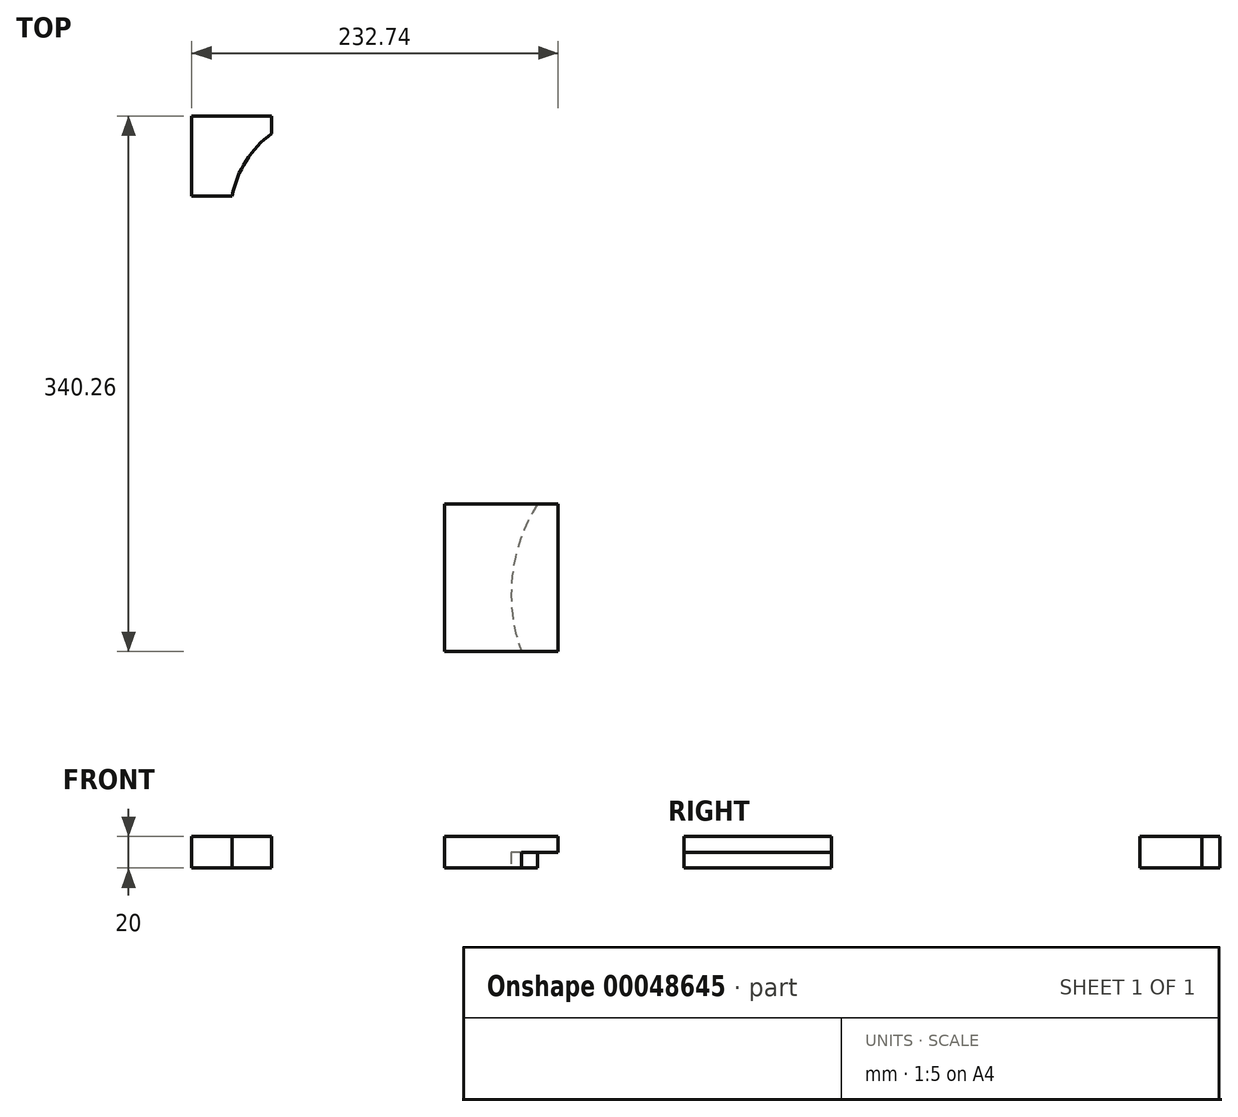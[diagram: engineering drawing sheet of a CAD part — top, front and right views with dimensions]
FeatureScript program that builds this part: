
annotation { "Feature Type Name" : "Feature", "Feature Type Description" : "" }
export const myFeature = defineFeature(function(context is Context, id is Id, definition is map)
    precondition{}
    {
        {
            assignVariable(context, id + "F0", {"name" : "teste", "anyValue" : 20});
        }
        {
            var Q0;
            Q0=qCreatedBy(makeId("Top.planeOp"),FACE);
            var sketch = newSketch(context, id + "F1", { "sketchPlane" : qUnion([Q0])});
            skLineSegment(sketch, "E0", {"start": v(-15.73, 9.77) * mm, "end": v(-15.73, -41.03) * mm});
            skLineSegment(sketch, "E1", {"start": v(-15.73, -41.03) * mm, "end": v(35.07, -41.03) * mm});
            skLineSegment(sketch, "E2", {"start": v(35.07, -41.03) * mm, "end": v(35.07, 9.77) * mm});
            skLineSegment(sketch, "E3", {"start": v(35.07, 9.77) * mm, "end": v(-15.73, 9.77) * mm});
            skLineSegment(sketch, "E4", {"start": v(178.54, 68) * mm, "end": v(178.54, -33.6) * mm});
            skLineSegment(sketch, "E5", {"start": v(178.54, -33.6) * mm, "end": v(407.14, -33.6) * mm});
            skLineSegment(sketch, "E6", {"start": v(407.14, -33.6) * mm, "end": v(407.14, 41.42) * mm});
            skLineSegment(sketch, "E7", {"start": v(407.14, 41.42) * mm, "end": v(381.74, 41.42) * mm});
            skLineSegment(sketch, "E8", {"start": v(381.74, 41.42) * mm, "end": v(381.74, -7.36) * mm});
            skLineSegment(sketch, "E9", {"start": v(381.74, -7.36) * mm, "end": v(305.54, -7.36) * mm});
            skLineSegment(sketch, "E10", {"start": v(305.54, -7.36) * mm, "end": v(305.54, 43.44) * mm});
            skLineSegment(sketch, "E11", {"start": v(305.54, 43.44) * mm, "end": v(280.14, 43.44) * mm});
            skLineSegment(sketch, "E12", {"start": v(280.14, 43.44) * mm, "end": v(280.14, -7.36) * mm});
            skLineSegment(sketch, "E13", {"start": v(280.14, -7.36) * mm, "end": v(203.94, -7.36) * mm});
            skLineSegment(sketch, "E14", {"start": v(203.94, -7.36) * mm, "end": v(203.94, 68) * mm});
            skLineSegment(sketch, "E15", {"start": v(203.94, 68) * mm, "end": v(178.54, 68) * mm});
            skSolve(sketch);
        }
        {
            var Q0;
            Q0=makeQuery(id+"F1.imprint","IMPRINT",FACE,{"disambiguationData":[TD([[makeQuery(id+"F1.imprint","IMPRINT",EDGE,{"derivedFrom":sQuery(id+"F1.wireOp",EDGE,"E0")}),1.0]])]});
            var Q1;
            Q1=sQuery(id+"F1.wireOp",EDGE,"E2");
            var Q2;
            Q2=sQuery(id+"F1.wireOp",EDGE,"E3");
            var Q3;
            Q3=sQuery(id+"F1.wireOp",EDGE,"E1");
            var Q4;
            Q4=sQuery(id+"F1.wireOp",EDGE,"E0");
            extrude(context, id + "F2", {"entities" : qUnion([Q0]), "surfaceEntities" : qUnion([Q1, Q2, Q3, Q4]), "depth" : (getVariable(context, 'teste')) * mm});
        }
        {
            var Q0;
            Q0=qCreatedBy(makeId("Top.planeOp"),FACE);
            var sketch = newSketch(context, id + "F3", { "sketchPlane" : qUnion([Q0])});
            skCircle(sketch, "E16", {"center": v(72.46, -52.8) * mm, "radius": 63.5 * mm});
            skSolve(sketch);
        }
        {
            var Q0;
            Q0=makeQuery(id+"F3.imprint","IMPRINT",FACE,{"disambiguationData":[TD([[makeQuery(id+"F3.imprint","IMPRINT",EDGE,{"derivedFrom":sQuery(id+"F3.wireOp",EDGE,"E16")}),1.0]])]});
            extrude(context, id + "F4", {"entities" : qUnion([Q0]), "operationType" : NewBodyOperationType.REMOVE, "depth" : 83.06 * mm});
        }
        {
            var Q0;
            Q0=qCreatedBy(makeId("Top.planeOp"),FACE);
            var sketch = newSketch(context, id + "F5", { "sketchPlane" : qUnion([Q0])});
            skLineSegment(sketch, "E17.bottom", {"start": v(144.9, -236.87) * mm, "end": v(217, -236.87) * mm});
            skLineSegment(sketch, "E17.top", {"start": v(144.9, -330.5) * mm, "end": v(217, -330.5) * mm});
            skLineSegment(sketch, "E17.left", {"start": v(144.9, -236.87) * mm, "end": v(144.9, -330.5) * mm});
            skLineSegment(sketch, "E17.right", {"start": v(217, -236.87) * mm, "end": v(217, -330.5) * mm});
            skSolve(sketch);
        }
        {
            var Q0;
            Q0=makeQuery(id+"F5.imprint","IMPRINT",FACE,{"disambiguationData":[TD([[makeQuery(id+"F5.imprint","IMPRINT",EDGE,{"derivedFrom":sQuery(id+"F5.wireOp",EDGE,"E17.bottom")}),-1.0]])]});
            extrude(context, id + "F6", {"entities" : qUnion([Q0]), "depth" : (getVariable(context, 'teste')) * mm});
        }
        {
            var Q0;
            Q0=qCreatedBy(makeId("Top.planeOp"),FACE);
            var sketch = newSketch(context, id + "F7", { "sketchPlane" : qUnion([Q0])});
            skCircle(sketch, "E18", {"center": v(293.12, -294.16) * mm, "radius": 105.92 * mm});
            skSolve(sketch);
        }
        {
            var Q0;
            Q0=makeQuery(id+"F7.imprint","IMPRINT",FACE,{"disambiguationData":[TD([[makeQuery(id+"F7.imprint","IMPRINT",EDGE,{"derivedFrom":sQuery(id+"F7.wireOp",EDGE,"E18")}),1.0]])]});
            extrude(context, id + "F8", {"entities" : qUnion([Q0]), "operationType" : NewBodyOperationType.REMOVE, "depth" : (getVariable(context, 'teste') / 2) * mm});
        }
    });
